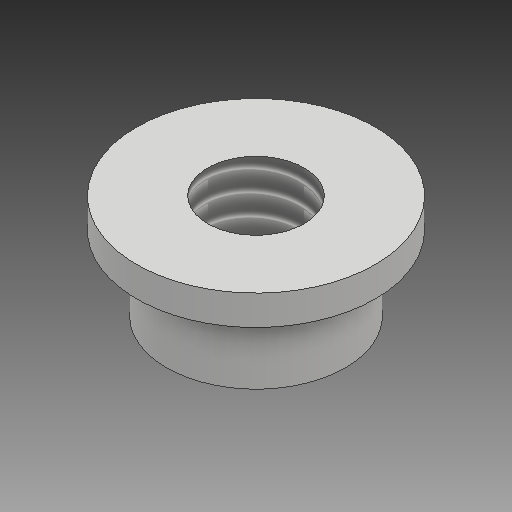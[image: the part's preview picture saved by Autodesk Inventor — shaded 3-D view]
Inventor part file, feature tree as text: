
AUTODESK INVENTOR PART (.ipt)
format: ipt  version: 2018 (Build 220112000, 112)  size: 112,640 bytes
history: native  units: mm
features: extrude x2, sketch x2, hole x1
ambient origin geometry x8: Origin, YZ Plane, XZ Plane, XY Plane, X Axis, Y Axis, Z Axis, Center Point
bodies: Volumenkörper1 (feature_tree)
feature tree (5):
  extrude  "Extrusion1"  Depth=2.5mm TaperAngle=0.0deg
  extrude  "Extrusion2"  Depth=1.0mm TaperAngle=0.0deg
  hole  "Bohrung1"  [1 undecoded]
  sketch  "Skizze1"  dims[d0=6.0mm d1=2.5mm d2=0.0mm]
  sketch  "Skizze2"  dims[d3=8.0mm d4=1.0mm d5=0.0mm d6=10.0mm d7=10.0mm d8=3.242mm d9=8.0mm d10=4.0mm d11=2.0mm d12=90.0deg d13=11.8mm d14=20.594885mm]
note: 1 required parameter value undecoded (feature->parameter linkage not recoverable at this tier; creation-order binding heuristic only, values carry confidence <= 0.55)
